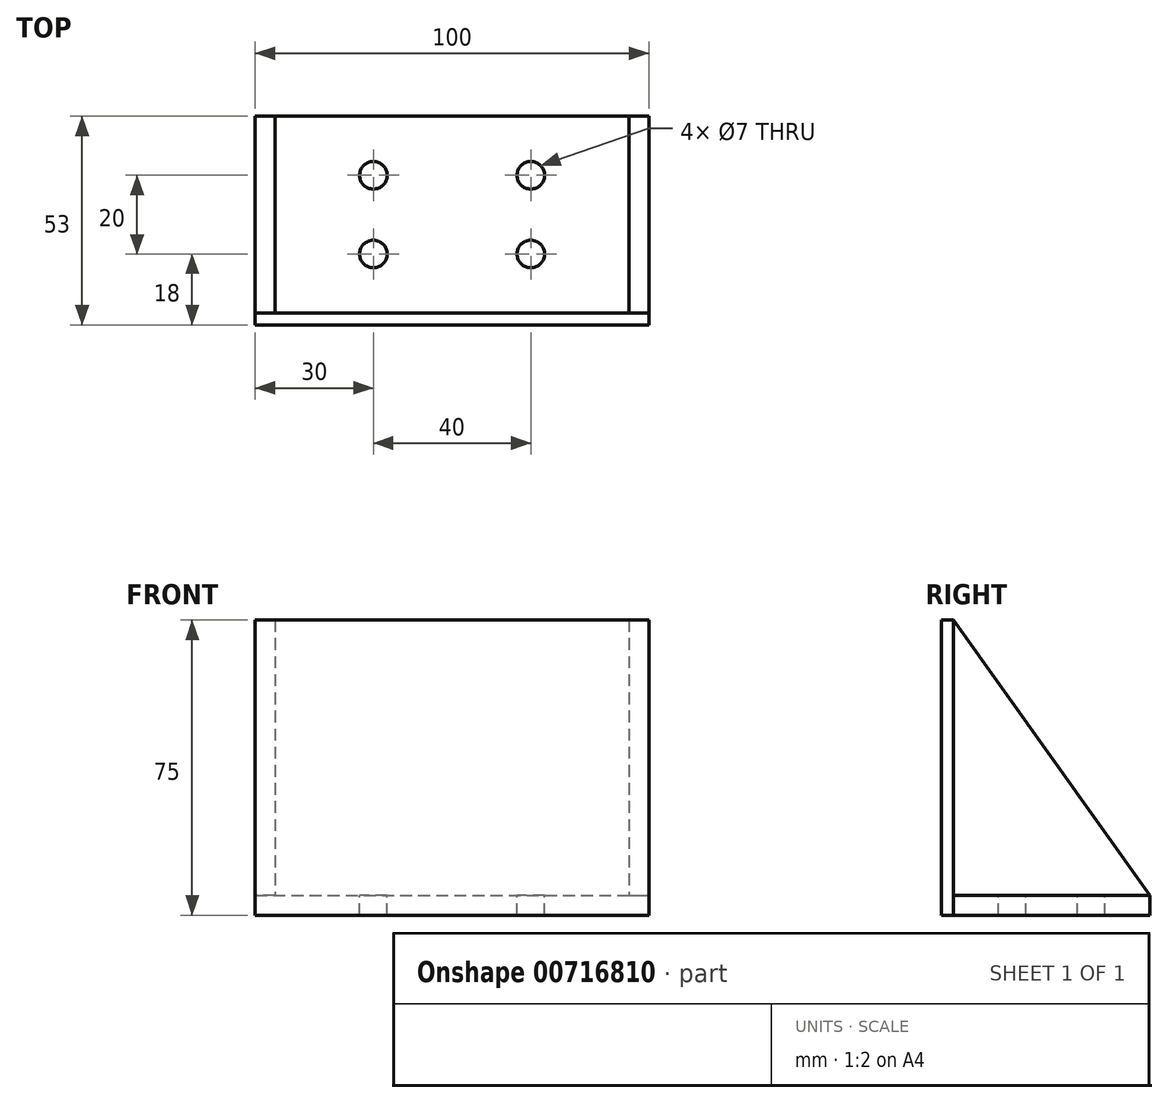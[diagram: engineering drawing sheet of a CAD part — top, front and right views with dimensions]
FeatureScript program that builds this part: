
annotation { "Feature Type Name" : "Feature", "Feature Type Description" : "" }
export const myFeature = defineFeature(function(context is Context, id is Id, definition is map)
    precondition{}
    {
        {
            var Q0;
            Q0=qCreatedBy(makeId("Top.planeOp"),FACE);
            var sketch = newSketch(context, id + "F0", { "sketchPlane" : qUnion([Q0])});
            skLineSegment(sketch, "E0.bottom", {"start": v(-50, 25) * mm, "end": v(50, 25) * mm});
            skLineSegment(sketch, "E0.top", {"start": v(-50, -25) * mm, "end": v(50, -25) * mm});
            skLineSegment(sketch, "E0.left", {"start": v(-50, 25) * mm, "end": v(-50, -25) * mm});
            skLineSegment(sketch, "E0.right", {"start": v(50, 25) * mm, "end": v(50, -25) * mm});
            skPoint(sketch, "E0.middle", {"position": v(0, 0) * mm});
            skSolve(sketch);
        }
        {
            var Q0;
            Q0 = qSketchRegion(id + "F0", true);
            extrude(context, id + "F1", {"entities" : qUnion([Q0]), "endBound" : BoundingType.SYMMETRIC, "depth" : 5 * mm, "offsetDistance" : 25 * mm});
        }
        {
            var Q0;
            Q0=makeQuery(id+"F1.opExtrude","SWEPT_FACE",FACE,{"disambiguationData":[OSD([sQuery(id+"F0.wireOp",EDGE,"E0.top")])]});
            var sketch = newSketch(context, id + "F2", { "sketchPlane" : qUnion([Q0])});
            skLineSegment(sketch, "E1.bottom", {"start": v(-50, -2.5) * mm, "end": v(50, -2.5) * mm});
            skLineSegment(sketch, "E1.top", {"start": v(-50, 72.5) * mm, "end": v(50, 72.5) * mm});
            skLineSegment(sketch, "E1.left", {"start": v(-50, -2.5) * mm, "end": v(-50, 72.5) * mm});
            skLineSegment(sketch, "E1.right", {"start": v(50, -2.5) * mm, "end": v(50, 72.5) * mm});
            skSolve(sketch);
        }
        {
            var Q0;
            {var subQ0=sQuery(id+"F2.wireOp",EDGE,"E1.top");Q0=makeQuery(id+"F2.imprint","IMPRINT",FACE,{"disambiguationData":[TD([[makeQuery(id+"F2.imprint","IMPRINT",EDGE,{"derivedFrom":subQ0}),-1.0]])]});}
            var Q1;
            {var subQ0=sQuery(id+"F2.wireOp",EDGE,"E1.bottom");Q1=makeQuery(id+"F2.imprint","IMPRINT",FACE,{"disambiguationData":[TD([[makeQuery(id+"F2.imprint","IMPRINT",EDGE,{"derivedFrom":subQ0}),1.0]])]});}
            extrude(context, id + "F3", {"entities" : qUnion([Q0, Q1]), "depth" : 3 * mm, "offsetDistance" : 25 * mm});
        }
        {
            var Q0;
            Q0=makeQuery(id+"F3.opExtrude","SWEPT_FACE",FACE,{"disambiguationData":[OSD([sQuery(id+"F2.wireOp",EDGE,"E1.right")])]});
            var sketch = newSketch(context, id + "F4", { "sketchPlane" : qUnion([Q0])});
            skLineSegment(sketch, "E2", {"start": v(-25, 72.5) * mm, "end": v(25, 2.5) * mm});
            skLineSegment(sketch, "E3", {"start": v(25, 2.5) * mm, "end": v(-25, 2.5) * mm});
            skLineSegment(sketch, "E4", {"start": v(-25, 2.5) * mm, "end": v(-25, 72.5) * mm});
            skSolve(sketch);
        }
        {
            var Q0;
            Q0 = qSketchRegion(id + "F4", true);
            extrude(context, id + "F5", {"entities" : qUnion([Q0]), "oppositeDirection" : true, "depth" : 5 * mm, "offsetDistance" : 25 * mm});
        }
        {
            var Q0;
            Q0=makeQuery(id+"F5.opExtrude","SWEPT_BODY",BODY,{"disambiguationData":[OSD([sQuery(id+"F4.wireOp",EDGE,"E2"),sQuery(id+"F4.wireOp",EDGE,"E3"),sQuery(id+"F4.wireOp",EDGE,"E4")])]});
            var Q1;
            Q1=qCreatedBy(makeId("Right.planeOp"),FACE);
            mirror(context, id + "F6", {"entities" : qUnion([Q0]), "mirrorPlane" : qUnion([Q1])});
        }
        {
            var Q0;
            Q0=makeQuery(id+"F1.opExtrude","CAP_FACE",FACE,{"disambiguationData":[OSD([sQuery(id+"F0.wireOp",EDGE,"E0.bottom"),sQuery(id+"F0.wireOp",EDGE,"E0.top"),sQuery(id+"F0.wireOp",EDGE,"E0.left"),sQuery(id+"F0.wireOp",EDGE,"E0.right")])],"isStart":false});
            var sketch = newSketch(context, id + "F7", { "sketchPlane" : qUnion([Q0])});
            skPoint(sketch, "E5", {"position": v(-20, 10) * mm});
            skPoint(sketch, "E6", {"position": v(20, 10) * mm});
            skPoint(sketch, "E7", {"position": v(-20, -10) * mm});
            skPoint(sketch, "E8", {"position": v(20, -10) * mm});
            skSolve(sketch);
        }
        {
            var Q0;
            Q0=sQuery(id+"F7.wireOp",VERTEX,"E7");
            var Q1;
            Q1=sQuery(id+"F7.wireOp",VERTEX,"E8");
            var Q2;
            Q2=sQuery(id+"F7.wireOp",VERTEX,"E5");
            var Q3;
            Q3=sQuery(id+"F7.wireOp",VERTEX,"E6");
            var Q4;
            Q4=makeQuery(id+"F1.opExtrude","SWEPT_BODY",BODY,{"disambiguationData":[OSD([sQuery(id+"F0.wireOp",EDGE,"E0.bottom"),sQuery(id+"F0.wireOp",EDGE,"E0.top"),sQuery(id+"F0.wireOp",EDGE,"E0.left"),sQuery(id+"F0.wireOp",EDGE,"E0.right")])]});
            hole(context, id + "F8", {"style" : HoleStyle.SIMPLE, "endStyle" : HoleEndStyle.THROUGH, "standardTappedOrClearance" : lookupTablePath({ "standard" : "ISO", "fit" : "Normal", "size" : "7", "type" : "Drilled" }), "standardBlindInLast" : lookupTablePath({ "fit" : "Standard", "standard" : "ISO", "size" : "7", "type" : "Drilled" }), "holeDiameter" : 7 * mm, "majorDiameter" : 5 * mm, "isTappedThrough" : true, "tappedDepth" : 12 * mm, "tapClearance" : 3, "locations" : qUnion([Q0, Q1, Q2, Q3]), "scope" : qUnion([Q4])});
        }
    });
